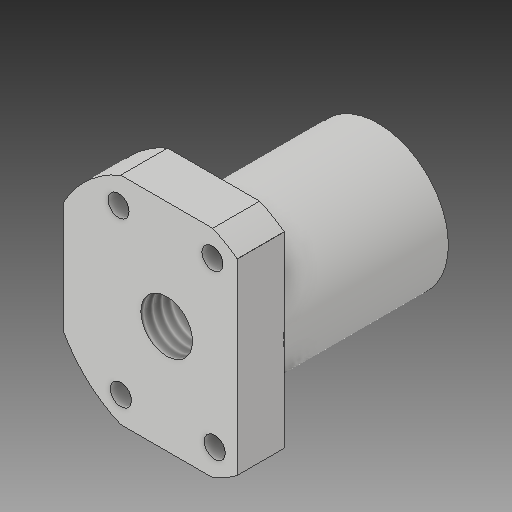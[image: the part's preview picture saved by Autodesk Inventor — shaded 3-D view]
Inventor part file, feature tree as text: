
AUTODESK INVENTOR PART (.ipt)
format: ipt  version: 2018 (Build 220112000, 112)  size: 208,384 bytes
history: native  units: mm
features: sketch x10, extrude x7, revolve x1, thread x1, plane x1
ambient origin geometry x8: Origin, YZ Plane, XZ Plane, XY Plane, X Axis, Y Axis, Z Axis, Center Point
bodies: Solid1 (feature_tree)
feature tree (20):
  revolve  "Revolution1"  [1 undecoded]
  extrude  "Extrusion1"  Depth=10.0mm
  extrude  "Extrusion2"  TaperAngle=90.0deg  [1 undecoded]
  thread  "Thread1"  [1 undecoded]
  extrude  "Extrusion3"  Depth=10.0mm TaperAngle=0.0deg
  plane  "Work Plane1"
  extrude  "Extrusion4"  Depth=10.0mm TaperAngle=0.0deg
  extrude  "Extrusion5"  Depth=15.0mm TaperAngle=0.0deg
  extrude  "Extrusion8"  Depth=8.0mm
  sketch  "Sketch21"  dims[d60=10.0mm d61=0.0mm d83=4.75mm d84=0.0mm]
  sketch  "Sketch22"  dims[d85=7.5mm]
  extrude  "Extrusion9"  Depth=10.0mm TaperAngle=0.0deg
  sketch  "Sketch1"  dims[d3=25.0mm d4=10.0mm]
  sketch  "Sketch2"  dims[d5=10.0mm d6=35.0mm]
  sketch  "Sketch3"  dims[d7=15.0mm d8=90.0deg d12=4.5mm]
  sketch  "Sketch4"  dims[d13=60.0mm d15=360.0deg d17=10.0mm d18=0.0mm]
  sketch  "Sketch5"  dims[d19=11.0mm d27=10.0mm d28=0.0mm]
  sketch  "Sketch9"  dims[d29=10.0mm d30=0.0mm d32=15.0mm d33=0.0mm]
  sketch  "Sketch20"  dims[d37=1.0mm d38=0.0mm d59=8.0mm]
  sketch  "Sketch23"  dims[d87=24.0mm d88=7.5mm d89=10.0mm d90=0.0mm d91=2.0mm]
note: 3 required parameter values undecoded (feature->parameter linkage not recoverable at this tier; creation-order binding heuristic only, values carry confidence <= 0.55)